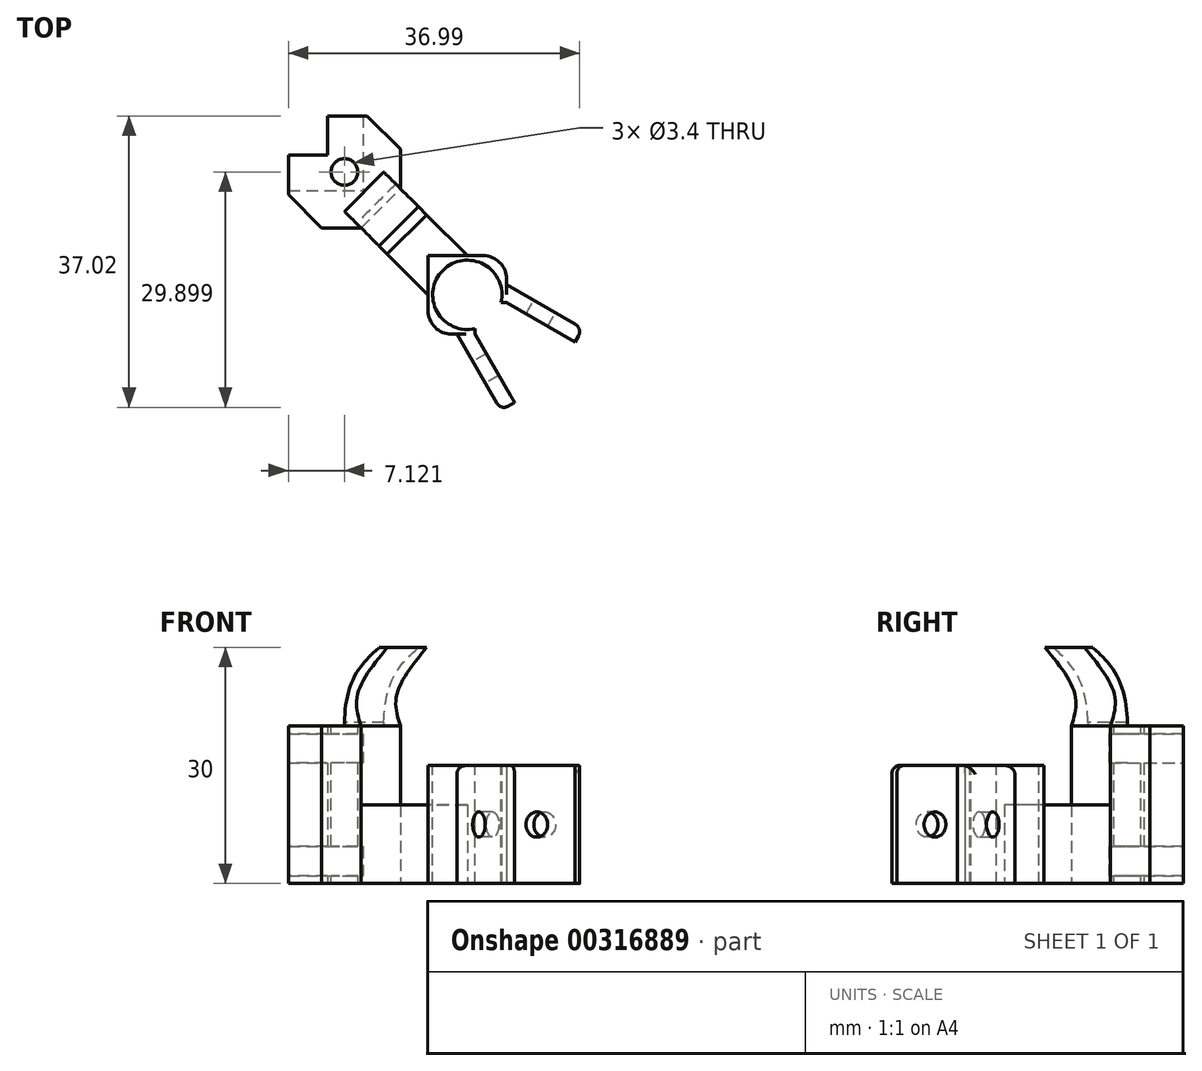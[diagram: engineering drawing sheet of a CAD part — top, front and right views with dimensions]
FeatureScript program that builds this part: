
annotation { "Feature Type Name" : "Feature", "Feature Type Description" : "" }
export const myFeature = defineFeature(function(context is Context, id is Id, definition is map)
    precondition{}
    {
        {
            var Q0;
            Q0=qCreatedBy(makeId("Top.planeOp"),FACE);
            var sketch = newSketch(context, id + "F0", { "sketchPlane" : qUnion([Q0])});
            skLineSegment(sketch, "E0", {"start": v(0, 0) * mm, "end": v(-5, 0) * mm});
            skLineSegment(sketch, "E1", {"start": v(-5, 0) * mm, "end": v(-5, 5) * mm});
            skLineSegment(sketch, "E2", {"start": v(-5, 5) * mm, "end": v(0, 5) * mm});
            skLineSegment(sketch, "E3", {"start": v(0, 5) * mm, "end": v(0, 10) * mm});
            skLineSegment(sketch, "E4", {"start": v(0, 10) * mm, "end": v(5, 10) * mm});
            skLineSegment(sketch, "E5", {"start": v(5, 10) * mm, "end": v(5, 5) * mm});
            skLineSegment(sketch, "E6", {"start": v(-5, 0) * mm, "end": v(-0.76, -4.24) * mm});
            skLineSegment(sketch, "E7", {"start": v(5, 10) * mm, "end": v(9.24, 5.76) * mm});
            skLineSegment(sketch, "E8", {"start": v(9.24, 5.76) * mm, "end": v(9.24, 0.76) * mm});
            skLineSegment(sketch, "E9", {"start": v(-0.76, -4.24) * mm, "end": v(4.24, -4.24) * mm});
            skLineSegment(sketch, "E10", {"start": v(9.24, 0.76) * mm, "end": v(17.73, -7.73) * mm});
            skLineSegment(sketch, "E11", {"start": v(4.24, -4.24) * mm, "end": v(12.73, -12.73) * mm});
            skLineSegment(sketch, "E12", {"start": v(12.73, -12.73) * mm, "end": v(12.73, -17.73) * mm});
            skLineSegment(sketch, "E13", {"start": v(12.73, -17.73) * mm, "end": v(22.73, -17.73) * mm});
            skLineSegment(sketch, "E14", {"start": v(22.73, -17.73) * mm, "end": v(22.73, -7.73) * mm});
            skLineSegment(sketch, "E15", {"start": v(22.73, -7.73) * mm, "end": v(17.73, -7.73) * mm});
            skLineSegment(sketch, "E16", {"start": v(4.24, -4.24) * mm, "end": v(9.24, 0.76) * mm});
            skPoint(sketch, "E17", {"position": v(22.73, -13.73) * mm});
            skPoint(sketch, "E18", {"position": v(18.73, -17.73) * mm});
            skLineSegment(sketch, "E19", {"start": v(22.73, -13.73) * mm, "end": v(31.39, -18.73) * mm});
            skLineSegment(sketch, "E20", {"start": v(18.73, -17.73) * mm, "end": v(23.73, -26.39) * mm});
            skLineSegment(sketch, "E21", {"start": v(31.39, -18.73) * mm, "end": v(32.39, -17) * mm});
            skLineSegment(sketch, "E22", {"start": v(32.39, -17) * mm, "end": v(22.73, -11.42) * mm});
            skLineSegment(sketch, "E23", {"start": v(23.73, -26.39) * mm, "end": v(22, -27.39) * mm});
            skLineSegment(sketch, "E24", {"start": v(22, -27.39) * mm, "end": v(16.42, -17.73) * mm});
            skSolve(sketch);
        }
        {
            var Q0;
            Q0=makeQuery(id+"F0.imprint","IMPRINT",FACE,{"disambiguationData":[TD([[makeQuery(id+"F0.imprint","IMPRINT",EDGE,{"derivedFrom":sQuery(id+"F0.wireOp",EDGE,"E1")}),-1.0]])]});
            extrude(context, id + "F1", {"entities" : qUnion([Q0]), "depth" : 20 * mm});
        }
        {
            var Q0;
            Q0=makeQuery(id+"F0.imprint","IMPRINT",FACE,{"disambiguationData":[TD([[makeQuery(id+"F0.imprint","IMPRINT",EDGE,{"derivedFrom":sQuery(id+"F0.wireOp",EDGE,"E10")}),-1.0]])]});
            extrude(context, id + "F2", {"entities" : qUnion([Q0]), "operationType" : NewBodyOperationType.ADD, "depth" : 10 * mm});
        }
        {
            var Q0;
            Q0=makeQuery(id+"F1.opExtrude","SWEPT_FACE",FACE,{"disambiguationData":[OSD([sQuery(id+"F0.wireOp",EDGE,"E4")])]});
            var sketch = newSketch(context, id + "F3", { "sketchPlane" : qUnion([Q0])});
            skPoint(sketch, "E25", {"position": v(0, 19) * mm});
            skPoint(sketch, "E26", {"position": v(0, 15.6) * mm});
            skPoint(sketch, "E27", {"position": v(0, 1) * mm});
            skPoint(sketch, "E28", {"position": v(0, 4.4) * mm});
            skLineSegment(sketch, "E29", {"start": v(0, 19) * mm, "end": v(-5, 19) * mm});
            skLineSegment(sketch, "E30", {"start": v(-5, 19) * mm, "end": v(-5, 15.6) * mm});
            skLineSegment(sketch, "E31", {"start": v(-5, 15.6) * mm, "end": v(0, 15.6) * mm});
            skSolve(sketch);
        }
        {
            var Q0;
            Q0=qSketchRegion(id+"F3",true);
            var Q1;
            {var subQ0=sQuery(id+"F3.wireOp",EDGE,"E29");Q1=makeQuery(id+"F3.imprint","IMPRINT",FACE,{"disambiguationData":[TD([[makeQuery(id+"F3.imprint","IMPRINT",EDGE,{"derivedFrom":subQ0}),1.0]])]});}
            extrude(context, id + "F4", {"entities" : qUnion([Q0, Q1]), "operationType" : NewBodyOperationType.REMOVE, "oppositeDirection" : true, "depth" : 25 * mm});
        }
        {
            var Q0;
            Q0=makeQuery(id+"F1.opExtrude","SWEPT_FACE",FACE,{"disambiguationData":[OSD([sQuery(id+"F0.wireOp",EDGE,"E2")])]});
            var sketch = newSketch(context, id + "F5", { "sketchPlane" : qUnion([Q0])});
            skLineSegment(sketch, "E32", {"start": v(0, 19) * mm, "end": v(5, 19) * mm});
            skLineSegment(sketch, "E33", {"start": v(5, 19) * mm, "end": v(5, 15.6) * mm});
            skLineSegment(sketch, "E34", {"start": v(5, 15.6) * mm, "end": v(0, 15.6) * mm});
            skLineSegment(sketch, "E35", {"start": v(0, 15.6) * mm, "end": v(0, 19) * mm});
            skSolve(sketch);
        }
        {
            var Q0;
            Q0=makeQuery(id+"F5.imprint","IMPRINT",FACE,{"disambiguationData":[TD([[makeQuery(id+"F5.imprint","IMPRINT",EDGE,{"derivedFrom":sQuery(id+"F5.wireOp",EDGE,"E32")}),-1.0]])]});
            extrude(context, id + "F6", {"entities" : qUnion([Q0]), "operationType" : NewBodyOperationType.REMOVE, "oppositeDirection" : true, "depth" : 25 * mm});
        }
        {
            var Q0;
            Q0=makeQuery(id+"F1.opExtrude","SWEPT_FACE",FACE,{"disambiguationData":[OSD([sQuery(id+"F0.wireOp",EDGE,"E7")])]});
            var sketch = newSketch(context, id + "F7", { "sketchPlane" : qUnion([Q0])});
            skLineSegment(sketch, "E36", {"start": v(3.54, 15.6) * mm, "end": v(-2.46, 15.6) * mm});
            skLineSegment(sketch, "E37", {"start": v(-2.46, 15.6) * mm, "end": v(-2.46, 19) * mm});
            skLineSegment(sketch, "E38", {"start": v(-2.46, 19) * mm, "end": v(3.54, 19) * mm});
            skLineSegment(sketch, "E39", {"start": v(3.54, 19) * mm, "end": v(3.54, 15.6) * mm});
            skSolve(sketch);
        }
        {
            var Q0;
            Q0=qSketchRegion(id+"F7",true);
            extrude(context, id + "F8", {"entities" : qUnion([Q0]), "operationType" : NewBodyOperationType.REMOVE, "oppositeDirection" : true, "depth" : 25 * mm});
        }
        {
            var Q0;
            {var subQ3=sQuery(id+"F0.wireOp",EDGE,"E4");Q0=makeQuery(id+"F4.boolean.opBoolean","SPLIT",FACE,{"disambiguationData":[TD([makeQuery(id+"F4.opExtrude","SWEPT_FACE",FACE,{"disambiguationData":[OSD([sQuery(id+"F3.wireOp",EDGE,"E31")])]})])],"derivedFrom":makeQuery(id+"F1.opExtrude","SWEPT_FACE",FACE,{"disambiguationData":[OSD([subQ3])]})});}
            var sketch = newSketch(context, id + "F9", { "sketchPlane" : qUnion([Q0])});
            skPoint(sketch, "E40", {"position": v(0, 1) * mm});
            skPoint(sketch, "E41", {"position": v(0, 4.4) * mm});
            skLineSegment(sketch, "E42.bottom", {"start": v(0, 4.4) * mm, "end": v(-5, 4.4) * mm});
            skLineSegment(sketch, "E42.top", {"start": v(0, 1) * mm, "end": v(-5, 1) * mm});
            skLineSegment(sketch, "E42.left", {"start": v(0, 4.4) * mm, "end": v(0, 1) * mm});
            skLineSegment(sketch, "E42.right", {"start": v(-5, 4.4) * mm, "end": v(-5, 1) * mm});
            skSolve(sketch);
        }
        {
            var Q0;
            Q0=qSketchRegion(id+"F9",true);
            extrude(context, id + "F10", {"entities" : qUnion([Q0]), "operationType" : NewBodyOperationType.REMOVE, "oppositeDirection" : true, "depth" : 25 * mm});
        }
        {
            var Q0;
            {var subQ3=sQuery(id+"F0.wireOp",EDGE,"E7");Q0=makeQuery(id+"F8.boolean.opBoolean","SPLIT",FACE,{"disambiguationData":[TD([makeQuery(id+"F4.boolean.opBoolean","COPY",FACE,{"derivedFrom":makeQuery(id+"F4.opExtrude","SWEPT_FACE",FACE,{"disambiguationData":[OSD([sQuery(id+"F3.wireOp",EDGE,"E31")])]})})])],"derivedFrom":makeQuery(id+"F1.opExtrude","SWEPT_FACE",FACE,{"disambiguationData":[OSD([subQ3])]})});}
            var sketch = newSketch(context, id + "F11", { "sketchPlane" : qUnion([Q0])});
            skLineSegment(sketch, "E43.bottom", {"start": v(3.54, 1) * mm, "end": v(-2.46, 1) * mm});
            skLineSegment(sketch, "E43.top", {"start": v(3.54, 4.4) * mm, "end": v(-2.46, 4.4) * mm});
            skLineSegment(sketch, "E43.left", {"start": v(3.54, 1) * mm, "end": v(3.54, 4.4) * mm});
            skLineSegment(sketch, "E43.right", {"start": v(-2.46, 1) * mm, "end": v(-2.46, 4.4) * mm});
            skSolve(sketch);
        }
        {
            var Q0;
            Q0=qSketchRegion(id+"F11",true);
            extrude(context, id + "F12", {"entities" : qUnion([Q0]), "operationType" : NewBodyOperationType.REMOVE, "oppositeDirection" : true, "depth" : 25 * mm});
        }
        {
            var Q0;
            {var subQ2=sQuery(id+"F0.wireOp",EDGE,"E2");Q0=makeQuery(id+"F6.boolean.opBoolean","SPLIT",FACE,{"disambiguationData":[TD([makeQuery(id+"F4.boolean.opBoolean","COPY",FACE,{"derivedFrom":makeQuery(id+"F4.opExtrude","SWEPT_FACE",FACE,{"disambiguationData":[OSD([sQuery(id+"F3.wireOp",EDGE,"E31")])]})})])],"derivedFrom":makeQuery(id+"F1.opExtrude","SWEPT_FACE",FACE,{"disambiguationData":[OSD([subQ2])]})});}
            var sketch = newSketch(context, id + "F13", { "sketchPlane" : qUnion([Q0])});
            skLineSegment(sketch, "E44.bottom", {"start": v(0, 4.4) * mm, "end": v(5, 4.4) * mm});
            skLineSegment(sketch, "E44.top", {"start": v(0, 1) * mm, "end": v(5, 1) * mm});
            skLineSegment(sketch, "E44.left", {"start": v(0, 4.4) * mm, "end": v(0, 1) * mm});
            skLineSegment(sketch, "E44.right", {"start": v(5, 4.4) * mm, "end": v(5, 1) * mm});
            skSolve(sketch);
        }
        {
            var Q0;
            Q0=qSketchRegion(id+"F13",true);
            extrude(context, id + "F14", {"entities" : qUnion([Q0]), "operationType" : NewBodyOperationType.REMOVE, "oppositeDirection" : true, "depth" : 25 * mm});
        }
        {
            var Q0;
            Q0=makeQuery(id+"F1.opExtrude","CAP_FACE",FACE,{"disambiguationData":[OSD([sQuery(id+"F0.wireOp",EDGE,"E1"),sQuery(id+"F0.wireOp",EDGE,"E2"),sQuery(id+"F0.wireOp",EDGE,"E3"),sQuery(id+"F0.wireOp",EDGE,"E4"),sQuery(id+"F0.wireOp",EDGE,"E6"),sQuery(id+"F0.wireOp",EDGE,"E7"),sQuery(id+"F0.wireOp",EDGE,"E8"),sQuery(id+"F0.wireOp",EDGE,"E9"),sQuery(id+"F0.wireOp",EDGE,"E16")])],"isStart":false});
            var sketch = newSketch(context, id + "F15", { "sketchPlane" : qUnion([Q0])});
            skLineSegment(sketch, "E45", {"start": v(0, 5) * mm, "end": v(0, 3.17) * mm});
            skLineSegment(sketch, "E46", {"start": v(0, 5) * mm, "end": v(2.05, 5) * mm});
            skLineSegment(sketch, "E47", {"start": v(0, 5) * mm, "end": v(2.12, 2.88) * mm});
            skSolve(sketch);
        }
        {
            var Q0;
            Q0=sQuery(id+"F15.wireOp",VERTEX,"E47.end");
            var Q1;
            Q1=makeQuery(id+"F1.opExtrude","SWEPT_BODY",BODY,{"disambiguationData":[OSD([sQuery(id+"F0.wireOp",EDGE,"E1"),sQuery(id+"F0.wireOp",EDGE,"E2"),sQuery(id+"F0.wireOp",EDGE,"E3"),sQuery(id+"F0.wireOp",EDGE,"E4"),sQuery(id+"F0.wireOp",EDGE,"E6"),sQuery(id+"F0.wireOp",EDGE,"E7"),sQuery(id+"F0.wireOp",EDGE,"E8"),sQuery(id+"F0.wireOp",EDGE,"E9"),sQuery(id+"F0.wireOp",EDGE,"E16")])]});
            hole(context, id + "F16", {"style" : HoleStyle.SIMPLE, "endStyle" : HoleEndStyle.THROUGH, "holeDiameter" : 3.4 * mm, "tappedDepth" : 12 * mm, "tapClearance" : 3, "locations" : qUnion([Q0]), "scope" : qUnion([Q1])});
        }
        {
            var Q0;
            Q0=makeQuery(id+"F2.opExtrude","CAP_FACE",FACE,{"disambiguationData":[OSD([sQuery(id+"F0.wireOp",EDGE,"E10"),sQuery(id+"F0.wireOp",EDGE,"E11"),sQuery(id+"F0.wireOp",EDGE,"E12"),sQuery(id+"F0.wireOp",EDGE,"E13"),sQuery(id+"F0.wireOp",EDGE,"E14"),sQuery(id+"F0.wireOp",EDGE,"E15"),sQuery(id+"F0.wireOp",EDGE,"E16")])],"isStart":false});
            var sketch = newSketch(context, id + "F17", { "sketchPlane" : qUnion([Q0])});
            skLineSegment(sketch, "E48", {"start": v(22.73, -7.73) * mm, "end": v(12.73, -17.73) * mm});
            skLineSegment(sketch, "E49", {"start": v(22.73, -17.73) * mm, "end": v(13.62, -8.62) * mm});
            skPoint(sketch, "E50", {"position": v(17.73, -12.73) * mm});
            skSolve(sketch);
        }
        {
            var Q0;
            Q0=sQuery(id+"F17.wireOp",VERTEX,"E50");
            var Q1;
            Q1=makeQuery(id+"F1.opExtrude","SWEPT_BODY",BODY,{"disambiguationData":[OSD([sQuery(id+"F0.wireOp",EDGE,"E1"),sQuery(id+"F0.wireOp",EDGE,"E2"),sQuery(id+"F0.wireOp",EDGE,"E3"),sQuery(id+"F0.wireOp",EDGE,"E4"),sQuery(id+"F0.wireOp",EDGE,"E6"),sQuery(id+"F0.wireOp",EDGE,"E7"),sQuery(id+"F0.wireOp",EDGE,"E8"),sQuery(id+"F0.wireOp",EDGE,"E9"),sQuery(id+"F0.wireOp",EDGE,"E16")])]});
            hole(context, id + "F18", {"style" : HoleStyle.SIMPLE, "endStyle" : HoleEndStyle.THROUGH, "holeDiameter" : 8.8 * mm, "tappedDepth" : 12 * mm, "tapClearance" : 3, "locations" : qUnion([Q0]), "scope" : qUnion([Q1])});
        }
        {
            var Q0;
            Q0=makeQuery(id+"F2.opExtrude","CAP_FACE",FACE,{"disambiguationData":[OSD([sQuery(id+"F0.wireOp",EDGE,"E10"),sQuery(id+"F0.wireOp",EDGE,"E11"),sQuery(id+"F0.wireOp",EDGE,"E12"),sQuery(id+"F0.wireOp",EDGE,"E13"),sQuery(id+"F0.wireOp",EDGE,"E14"),sQuery(id+"F0.wireOp",EDGE,"E15"),sQuery(id+"F0.wireOp",EDGE,"E16")])],"isStart":false});
            var sketch = newSketch(context, id + "F19", { "sketchPlane" : qUnion([Q0])});
            skLineSegment(sketch, "E51.bottom", {"start": v(22.73, -7.73) * mm, "end": v(12.73, -7.73) * mm});
            skLineSegment(sketch, "E51.top", {"start": v(22.73, -17.73) * mm, "end": v(12.73, -17.73) * mm});
            skLineSegment(sketch, "E51.left", {"start": v(22.73, -7.73) * mm, "end": v(22.73, -17.73) * mm});
            skLineSegment(sketch, "E51.right", {"start": v(12.73, -7.73) * mm, "end": v(12.73, -17.73) * mm});
            skSolve(sketch);
        }
        {
            var Q0;
            {var subQ1=sQuery(id+"F19.wireOp",EDGE,"E51.top");Q0=makeQuery(id+"F19.imprint","IMPRINT",FACE,{"disambiguationData":[TD([[makeQuery(id+"F19.imprint","IMPRINT",EDGE,{"derivedFrom":subQ1}),1.0]])]});}
            extrude(context, id + "F20", {"entities" : qUnion([Q0]), "operationType" : NewBodyOperationType.ADD, "depth" : 5 * mm});
        }
        {
            var Q0;
            Q0=makeQuery(id+"F8.boolean.opBoolean","MERGE",FACE,{"derivedFrom":[makeQuery(id+"F6.boolean.opBoolean","MERGE",FACE,{"derivedFrom":[makeQuery(id+"F4.boolean.opBoolean","COPY",FACE,{"derivedFrom":makeQuery(id+"F4.opExtrude","SWEPT_FACE",FACE,{"disambiguationData":[OSD([sQuery(id+"F3.wireOp",EDGE,"E31")])]})}),makeQuery(id+"F6.opExtrude","SWEPT_FACE",FACE,{"disambiguationData":[OSD([sQuery(id+"F5.wireOp",EDGE,"E34")])]})]}),makeQuery(id+"F8.opExtrude","SWEPT_FACE",FACE,{"disambiguationData":[OSD([sQuery(id+"F7.wireOp",EDGE,"E36")])]})]});
            extrude(context, id + "F21", {"entities" : qUnion([Q0]), "operationType" : NewBodyOperationType.REMOVE, "oppositeDirection" : true, "depth" : 0.3 * mm});
        }
        {
            var Q0;
            Q0=makeQuery(id+"F14.boolean.opBoolean","MERGE",FACE,{"derivedFrom":[makeQuery(id+"F12.boolean.opBoolean","MERGE",FACE,{"derivedFrom":[makeQuery(id+"F10.boolean.opBoolean","COPY",FACE,{"derivedFrom":makeQuery(id+"F10.opExtrude","SWEPT_FACE",FACE,{"disambiguationData":[OSD([sQuery(id+"F9.wireOp",EDGE,"E42.bottom")])]})}),makeQuery(id+"F12.opExtrude","SWEPT_FACE",FACE,{"disambiguationData":[OSD([sQuery(id+"F11.wireOp",EDGE,"E43.top")])]})]}),makeQuery(id+"F14.opExtrude","SWEPT_FACE",FACE,{"disambiguationData":[OSD([sQuery(id+"F13.wireOp",EDGE,"E44.bottom")])]})]});
            extrude(context, id + "F22", {"entities" : qUnion([Q0]), "operationType" : NewBodyOperationType.REMOVE, "oppositeDirection" : true, "depth" : 0.3 * mm});
        }
        {
            var Q0;
            Q0=makeQuery(id+"F20.boolean.opBoolean","MERGE",FACE,{"derivedFrom":[makeQuery(id+"F2.opExtrude","SWEPT_FACE",FACE,{"disambiguationData":[OSD([sQuery(id+"F0.wireOp",EDGE,"E13")])]}),makeQuery(id+"F20.opExtrude","SWEPT_FACE",FACE,{"disambiguationData":[OSD([sQuery(id+"F19.wireOp",EDGE,"E51.top")])]})]});
            var sketch = newSketch(context, id + "F23", { "sketchPlane" : qUnion([Q0])});
            skLineSegment(sketch, "E52", {"start": v(12.79, 15) * mm, "end": v(22.73, 15) * mm});
            skPoint(sketch, "E53", {"position": v(18.73, 15) * mm});
            skLineSegment(sketch, "E54", {"start": v(18.73, 15) * mm, "end": v(18.73, 0) * mm});
            skLineSegment(sketch, "E55", {"start": v(18.73, 0) * mm, "end": v(22.73, 0) * mm});
            skLineSegment(sketch, "E56", {"start": v(22.73, 0) * mm, "end": v(22.73, 15) * mm});
            skSolve(sketch);
        }
        {
            var Q0;
            Q0=makeQuery(id+"F20.boolean.opBoolean","MERGE",FACE,{"derivedFrom":[makeQuery(id+"F2.opExtrude","SWEPT_FACE",FACE,{"disambiguationData":[OSD([sQuery(id+"F0.wireOp",EDGE,"E14")])]}),makeQuery(id+"F20.opExtrude","SWEPT_FACE",FACE,{"disambiguationData":[OSD([sQuery(id+"F19.wireOp",EDGE,"E51.left")])]})]});
            var sketch = newSketch(context, id + "F24", { "sketchPlane" : qUnion([Q0])});
            skLineSegment(sketch, "E57", {"start": v(-17.73, 15) * mm, "end": v(-7.73, 15) * mm});
            skPoint(sketch, "E58", {"position": v(-13.73, 15) * mm});
            skLineSegment(sketch, "E59", {"start": v(-13.73, 15) * mm, "end": v(-13.73, 0) * mm});
            skLineSegment(sketch, "E60", {"start": v(-13.73, 0) * mm, "end": v(-17.73, 0) * mm});
            skLineSegment(sketch, "E61", {"start": v(-17.73, 0) * mm, "end": v(-17.73, 15) * mm});
            skSolve(sketch);
        }
        {
            var Q0;
            Q0=qSketchRegion(id+"F24",true);
            extrude(context, id + "F25", {"entities" : qUnion([Q0]), "operationType" : NewBodyOperationType.REMOVE, "oppositeDirection" : true, "depth" : 2.4 * mm});
        }
        {
            var Q0;
            Q0=qSketchRegion(id+"F23",true);
            extrude(context, id + "F26", {"entities" : qUnion([Q0]), "operationType" : NewBodyOperationType.REMOVE, "oppositeDirection" : true, "depth" : 3.85 * mm});
        }
        {
            var Q0;
            Q0=makeQuery(id+"F20.boolean.opBoolean","MERGE",EDGE,{"derivedFrom":[makeQuery(id+"F2.opExtrude","SWEPT_EDGE",EDGE,{"disambiguationData":[OSD([sQuery(id+"F0.wireOp",EDGE,"E14"),sQuery(id+"F0.wireOp",EDGE,"E15")])]}),makeQuery(id+"F20.opExtrude","SWEPT_EDGE",EDGE,{"disambiguationData":[OSD([sQuery(id+"F19.wireOp",EDGE,"E51.bottom"),sQuery(id+"F19.wireOp",EDGE,"E51.left")])]})]});
            fillet(context, id + "F27", {"entities" : qUnion([Q0]), "radius" : 3 * mm, "tangentPropagation" : true, "allowEdgeOverflow" : false});
        }
        {
            var Q0;
            Q0=makeQuery(id+"F20.boolean.opBoolean","MERGE",EDGE,{"derivedFrom":[makeQuery(id+"F2.opExtrude","SWEPT_EDGE",EDGE,{"disambiguationData":[OSD([sQuery(id+"F0.wireOp",EDGE,"E12"),sQuery(id+"F0.wireOp",EDGE,"E13")])]}),makeQuery(id+"F20.opExtrude","SWEPT_EDGE",EDGE,{"disambiguationData":[OSD([sQuery(id+"F19.wireOp",EDGE,"E51.top"),sQuery(id+"F19.wireOp",EDGE,"E51.right")])]})]});
            fillet(context, id + "F28", {"entities" : qUnion([Q0]), "radius" : 3 * mm, "tangentPropagation" : true, "allowEdgeOverflow" : false});
        }
        {
            var Q0;
            Q0=makeQuery(id+"F21.boolean.opBoolean","COPY",FACE,{"derivedFrom":makeQuery(id+"F21.opExtrude","CAP_FACE",FACE,{"disambiguationData":[OSD([sQuery(id+"F3.wireOp",EDGE,"E31"),sQuery(id+"F5.wireOp",EDGE,"E34"),sQuery(id+"F7.wireOp",EDGE,"E36")])],"isStart":false})});
            var sketch = newSketch(context, id + "F29", { "sketchPlane" : qUnion([Q0])});
            skLineSegment(sketch, "E62", {"start": v(4.45, 0.55) * mm, "end": v(-5, 0.55) * mm});
            skLineSegment(sketch, "E63", {"start": v(4.45, 0.55) * mm, "end": v(4.45, 10) * mm});
            skSolve(sketch);
        }
        {
            var Q0;
            {var subQ6=sQuery(id+"F29.wireOp",EDGE,"E62");Q0=makeQuery(id+"F29.imprint","IMPRINT",FACE,{"disambiguationData":[TD([[makeQuery(id+"F29.imprint","IMPRINT",EDGE,{"derivedFrom":subQ6}),1.0]])]});}
            extrude(context, id + "F30", {"entities" : qUnion([Q0]), "operationType" : NewBodyOperationType.ADD, "depth" : 4 * mm, "hasSecondDirection" : true, "secondDirectionOppositeDirection" : true, "secondDirectionDepth" : 14.72 * mm});
        }
        {
            var Q0;
            {var subQ1=sQuery(id+"F0.wireOp",EDGE,"E9");Q0=makeQuery(id+"F30.boolean.opBoolean","SPLIT",FACE,{"disambiguationData":[TD([makeQuery(id+"F1.opExtrude","SWEPT_FACE",FACE,{"disambiguationData":[OSD([subQ1])]})])],"derivedFrom":makeQuery(id+"F14.boolean.opBoolean","MERGE",FACE,{"derivedFrom":[makeQuery(id+"F12.boolean.opBoolean","MERGE",FACE,{"derivedFrom":[makeQuery(id+"F10.boolean.opBoolean","COPY",FACE,{"derivedFrom":makeQuery(id+"F10.opExtrude","SWEPT_FACE",FACE,{"disambiguationData":[OSD([sQuery(id+"F9.wireOp",EDGE,"E42.top")])]})}),makeQuery(id+"F12.opExtrude","SWEPT_FACE",FACE,{"disambiguationData":[OSD([sQuery(id+"F11.wireOp",EDGE,"E43.bottom")])]})]}),makeQuery(id+"F14.opExtrude","SWEPT_FACE",FACE,{"disambiguationData":[OSD([sQuery(id+"F13.wireOp",EDGE,"E44.top")])]})]})});}
            extrude(context, id + "F31", {"entities" : qUnion([Q0]), "operationType" : NewBodyOperationType.ADD, "depth" : 4.73 * mm});
        }
        {
            var Q0;
            {var subQ0=sQuery(id+"F0.wireOp",EDGE,"E20");Q0=makeQuery(id+"F0.imprint","IMPRINT",FACE,{"disambiguationData":[TD([[makeQuery(id+"F0.imprint","IMPRINT",EDGE,{"derivedFrom":subQ0}),-1.0]])]});}
            var Q1;
            {var subQ0=sQuery(id+"F0.wireOp",EDGE,"E19");Q1=makeQuery(id+"F0.imprint","IMPRINT",FACE,{"disambiguationData":[TD([[makeQuery(id+"F0.imprint","IMPRINT",EDGE,{"derivedFrom":subQ0}),1.0]])]});}
            extrude(context, id + "F32", {"entities" : qUnion([Q0, Q1]), "operationType" : NewBodyOperationType.ADD, "depth" : 15 * mm});
        }
        {
            var Q0;
            Q0=makeQuery(id+"F32.opExtrude","SWEPT_FACE",FACE,{"disambiguationData":[OSD([sQuery(id+"F0.wireOp",EDGE,"E22")])]});
            var sketch = newSketch(context, id + "F33", { "sketchPlane" : qUnion([Q0])});
            skLineSegment(sketch, "E64", {"start": v(-25.4, 15) * mm, "end": v(-36.55, 0) * mm});
            skLineSegment(sketch, "E65", {"start": v(-36.55, 15) * mm, "end": v(-25.4, 0) * mm});
            skPoint(sketch, "E66", {"position": v(-30.97, 7.5) * mm});
            skSolve(sketch);
        }
        {
            var Q0;
            Q0=sQuery(id+"F33.wireOp",VERTEX,"E66");
            var Q1;
            Q1=makeQuery(id+"F1.opExtrude","SWEPT_BODY",BODY,{"disambiguationData":[OSD([sQuery(id+"F0.wireOp",EDGE,"E1"),sQuery(id+"F0.wireOp",EDGE,"E2"),sQuery(id+"F0.wireOp",EDGE,"E3"),sQuery(id+"F0.wireOp",EDGE,"E4"),sQuery(id+"F0.wireOp",EDGE,"E6"),sQuery(id+"F0.wireOp",EDGE,"E7"),sQuery(id+"F0.wireOp",EDGE,"E8"),sQuery(id+"F0.wireOp",EDGE,"E9"),sQuery(id+"F0.wireOp",EDGE,"E16")])]});
            hole(context, id + "F34", {"style" : HoleStyle.SIMPLE, "endStyle" : HoleEndStyle.BLIND, "holeDiameter" : 3.2 * mm, "holeDepth" : 5 * mm, "tappedDepth" : 12 * mm, "tapClearance" : 3, "locations" : qUnion([Q0]), "scope" : qUnion([Q1])});
        }
        {
            var Q0;
            Q0=makeQuery(id+"F32.opExtrude","SWEPT_FACE",FACE,{"disambiguationData":[OSD([sQuery(id+"F0.wireOp",EDGE,"E24")])]});
            var sketch = newSketch(context, id + "F35", { "sketchPlane" : qUnion([Q0])});
            skLineSegment(sketch, "E67", {"start": v(23.56, 15) * mm, "end": v(34.72, 0) * mm});
            skLineSegment(sketch, "E68", {"start": v(34.72, 15) * mm, "end": v(23.56, 0) * mm});
            skPoint(sketch, "E69", {"position": v(29.14, 7.5) * mm});
            skSolve(sketch);
        }
        {
            var Q0;
            Q0=sQuery(id+"F35.wireOp",VERTEX,"E69");
            var Q1;
            Q1=makeQuery(id+"F1.opExtrude","SWEPT_BODY",BODY,{"disambiguationData":[OSD([sQuery(id+"F0.wireOp",EDGE,"E1"),sQuery(id+"F0.wireOp",EDGE,"E2"),sQuery(id+"F0.wireOp",EDGE,"E3"),sQuery(id+"F0.wireOp",EDGE,"E4"),sQuery(id+"F0.wireOp",EDGE,"E6"),sQuery(id+"F0.wireOp",EDGE,"E7"),sQuery(id+"F0.wireOp",EDGE,"E8"),sQuery(id+"F0.wireOp",EDGE,"E9"),sQuery(id+"F0.wireOp",EDGE,"E16")])]});
            hole(context, id + "F36", {"style" : HoleStyle.SIMPLE, "endStyle" : HoleEndStyle.BLIND, "holeDiameter" : 3.2 * mm, "holeDepth" : 5 * mm, "tappedDepth" : 12 * mm, "tapClearance" : 3, "locations" : qUnion([Q0]), "scope" : qUnion([Q1])});
        }
        {
            var Q0;
            Q0=makeQuery(id+"F32.opExtrude","CAP_EDGE",EDGE,{"disambiguationData":[OSD([sQuery(id+"F0.wireOp",EDGE,"E24")])],"isStart":false});
            fillet(context, id + "F37", {"entities" : qUnion([Q0]), "radius" : 1 * mm, "tangentPropagation" : true, "allowEdgeOverflow" : false});
        }
        {
            var Q0;
            Q0=makeQuery(id+"F32.opExtrude","SWEPT_EDGE",EDGE,{"disambiguationData":[OSD([sQuery(id+"F0.wireOp",EDGE,"E23"),sQuery(id+"F0.wireOp",EDGE,"E24")])]});
            fillet(context, id + "F38", {"entities" : qUnion([Q0]), "radius" : 1 * mm, "tangentPropagation" : true, "allowEdgeOverflow" : false});
        }
        {
            var Q0;
            Q0=makeQuery(id+"F32.opExtrude","CAP_EDGE",EDGE,{"disambiguationData":[OSD([sQuery(id+"F0.wireOp",EDGE,"E22")])],"isStart":false});
            var Q1;
            Q1=makeQuery(id+"F32.opExtrude","SWEPT_EDGE",EDGE,{"disambiguationData":[OSD([sQuery(id+"F0.wireOp",EDGE,"E21"),sQuery(id+"F0.wireOp",EDGE,"E22")])]});
            fillet(context, id + "F39", {"entities" : qUnion([Q0, Q1]), "radius" : 1.1 * mm, "tangentPropagation" : true, "allowEdgeOverflow" : false});
        }
        {
            var Q0;
            Q0=makeQuery(id+"F1.opExtrude","CAP_FACE",FACE,{"disambiguationData":[OSD([sQuery(id+"F0.wireOp",EDGE,"E1"),sQuery(id+"F0.wireOp",EDGE,"E2"),sQuery(id+"F0.wireOp",EDGE,"E3"),sQuery(id+"F0.wireOp",EDGE,"E4"),sQuery(id+"F0.wireOp",EDGE,"E6"),sQuery(id+"F0.wireOp",EDGE,"E7"),sQuery(id+"F0.wireOp",EDGE,"E8"),sQuery(id+"F0.wireOp",EDGE,"E9"),sQuery(id+"F0.wireOp",EDGE,"E16")])],"isStart":false});
            var sketch = newSketch(context, id + "F40", { "sketchPlane" : qUnion([Q0])});
            skLineSegment(sketch, "E70", {"start": v(9.24, 0.76) * mm, "end": v(7.12, 2.88) * mm});
            skLineSegment(sketch, "E71", {"start": v(4.24, -4.24) * mm, "end": v(2.12, -2.12) * mm});
            skLineSegment(sketch, "E72", {"start": v(2.12, -2.12) * mm, "end": v(7.12, 2.88) * mm});
            skLineSegment(sketch, "E73", {"start": v(9.24, 0.76) * mm, "end": v(4.24, -4.24) * mm});
            skSolve(sketch);
        }
        {
            var Q0;
            Q0=makeQuery(id+"F40.imprint","IMPRINT",FACE,{"disambiguationData":[TD([[makeQuery(id+"F40.imprint","IMPRINT",EDGE,{"derivedFrom":sQuery(id+"F40.wireOp",EDGE,"E70")}),1.0]])]});
            extrude(context, id + "F41", {"entities" : qUnion([Q0]), "operationType" : NewBodyOperationType.ADD, "depth" : 10 * mm});
        }
        {
            var Q0;
            {var subQ0=sQuery(id+"F0.wireOp",EDGE,"E16");Q0=makeQuery(id+"F41.boolean.opBoolean","MERGE",FACE,{"derivedFrom":[makeQuery(id+"F30.boolean.opBoolean","MERGE",FACE,{"derivedFrom":[makeQuery(id+"F1.opExtrude","SWEPT_FACE",FACE,{"disambiguationData":[OSD([subQ0])]}),makeQuery(id+"F30.opExtrude","SWEPT_FACE",FACE,{"disambiguationData":[OSD([subQ0,sQuery(id+"F3.wireOp",EDGE,"E31")])]})]}),makeQuery(id+"F41.opExtrude","SWEPT_FACE",FACE,{"disambiguationData":[OSD([sQuery(id+"F40.wireOp",EDGE,"E73")])]})]});}
            var sketch = newSketch(context, id + "F42", { "sketchPlane" : qUnion([Q0])});
            skLineSegment(sketch, "E74", {"start": v(7.07, 30) * mm, "end": v(0, 30) * mm});
            skLineSegment(sketch, "E75", {"start": v(0, 30) * mm, "end": v(0, 20) * mm});
            skLineSegment(sketch, "E76", {"start": v(0, 20) * mm, "end": v(7.07, 20) * mm});
            skLineSegment(sketch, "E77", {"start": v(7.07, 20) * mm, "end": v(7.07, 30) * mm});
            skSolve(sketch);
        }
        {
            var Q0;
            Q0=makeQuery(id+"F42.imprint","IMPRINT",FACE,{"disambiguationData":[TD([[makeQuery(id+"F42.imprint","IMPRINT",EDGE,{"derivedFrom":sQuery(id+"F42.wireOp",EDGE,"E74")}),-1.0]])]});
            extrude(context, id + "F43", {"entities" : qUnion([Q0]), "operationType" : NewBodyOperationType.ADD, "depth" : 4.7 * mm});
        }
        {
            var Q0;
            Q0=makeQuery(id+"F43.boolean.opBoolean","MERGE",FACE,{"derivedFrom":[makeQuery(id+"F41.opExtrude","SWEPT_FACE",FACE,{"disambiguationData":[OSD([sQuery(id+"F40.wireOp",EDGE,"E71")])]}),makeQuery(id+"F43.opExtrude","SWEPT_FACE",FACE,{"disambiguationData":[OSD([sQuery(id+"F42.wireOp",EDGE,"E75")])]})]});
            var sketch = newSketch(context, id + "F44", { "sketchPlane" : qUnion([Q0])});
            skLineSegment(sketch, "E78", {"start": v(10.7, 28.65) * mm, "end": v(10.7, 30) * mm});
            skLineSegment(sketch, "E79", {"start": v(10.7, 30) * mm, "end": v(3, 30) * mm});
            skLineSegment(sketch, "E80", {"start": v(3, 30) * mm, "end": v(3, 27.84) * mm});
            skLineSegment(sketch, "E81", {"start": v(3, 20) * mm, "end": v(6, 20) * mm});
            skLineSegment(sketch, "E82", {"start": v(8.24, 30) * mm, "end": v(10.7, 30) * mm});
            skFitSpline(sketch, "E83", {"points": [v(6, 20) * mm, v(5.27, 23.8) * mm, v(10.7, 30) * mm], "startDerivative": vector(-4.03, 9.12) * mm, "endDerivative": vector(12.4, 10.78) * mm});
            skFitSpline(sketch, "E84", {"points": [v(3, 20) * mm, v(5.28, 26.9) * mm, v(9.23, 30) * mm], "startDerivative": vector(-0.23, 13.05) * mm, "endDerivative": vector(2.34, 1.84) * mm});
            skSolve(sketch);
        }
        {
            var Q0;
            {var subQ0=sQuery(id+"F44.wireOp",EDGE,"E79");Q0=makeQuery(id+"F44.imprint","IMPRINT",FACE,{"disambiguationData":[TD([[makeQuery(id+"F44.imprint","IMPRINT",EDGE,{"derivedFrom":subQ0}),1.0]])]});}
            extrude(context, id + "F45", {"entities" : qUnion([Q0]), "operationType" : NewBodyOperationType.REMOVE, "oppositeDirection" : true, "depth" : 25 * mm});
        }
        {
            var Q0;
            {var subQ0=sQuery(id+"F44.wireOp",EDGE,"E78");Q0=makeQuery(id+"F44.imprint","IMPRINT",FACE,{"disambiguationData":[TD([[makeQuery(id+"F44.imprint","IMPRINT",EDGE,{"derivedFrom":subQ0}),-1.0]])]});}
            extrude(context, id + "F46", {"entities" : qUnion([Q0]), "operationType" : NewBodyOperationType.REMOVE, "oppositeDirection" : true, "depth" : 25 * mm});
        }
    });
